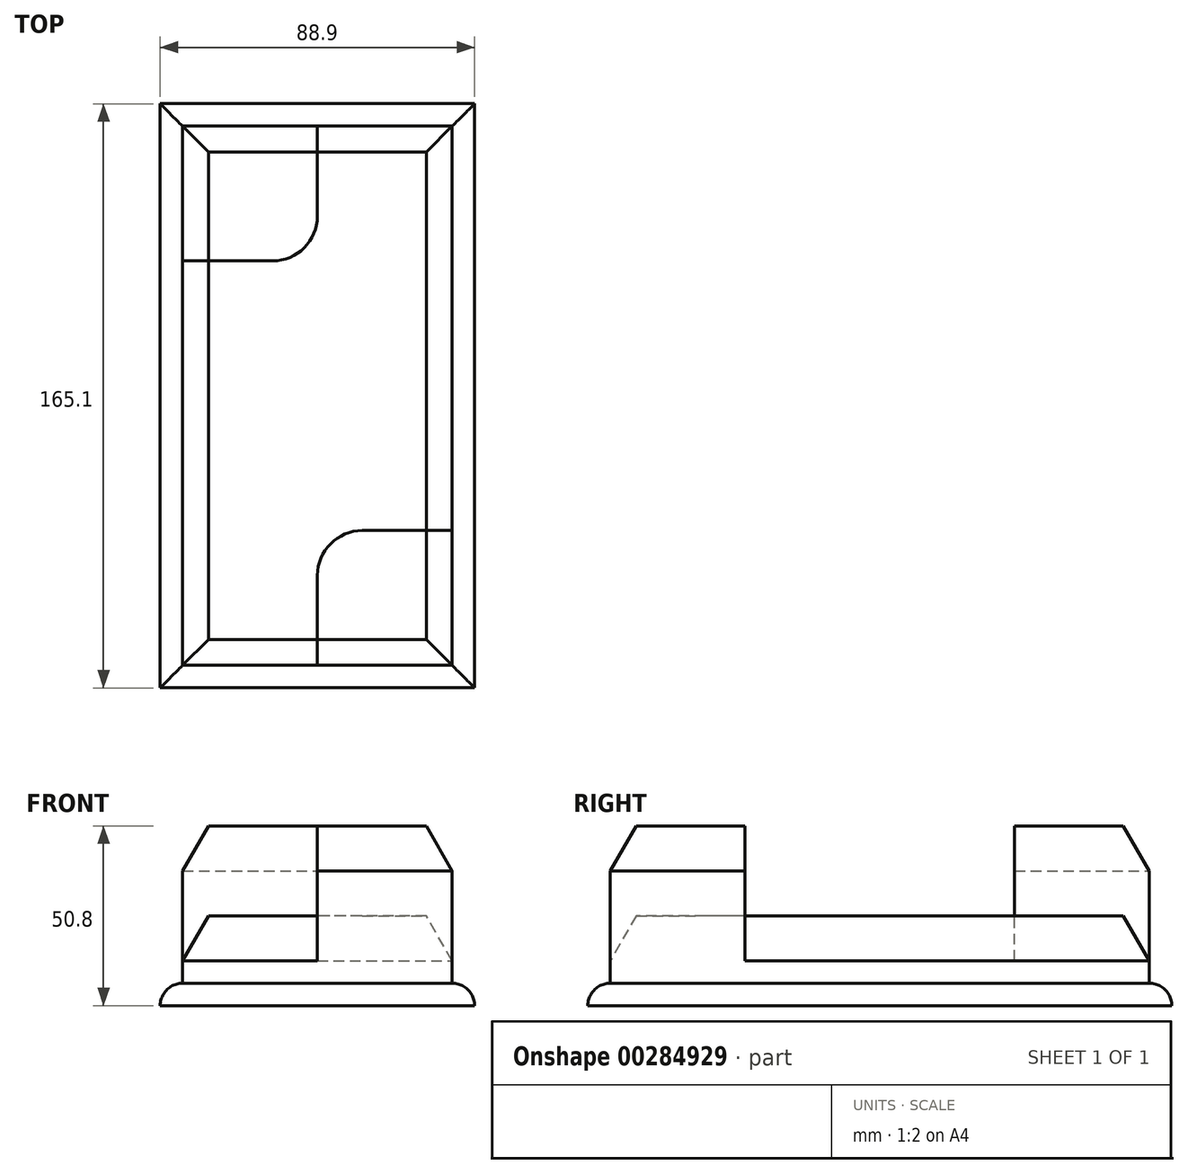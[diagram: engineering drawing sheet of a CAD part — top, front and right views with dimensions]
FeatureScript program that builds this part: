
annotation { "Feature Type Name" : "Feature", "Feature Type Description" : "" }
export const myFeature = defineFeature(function(context is Context, id is Id, definition is map)
    precondition{}
    {
        {
            var Q0;
            Q0=qCreatedBy(makeId("Top.planeOp"),FACE);
            var sketch = newSketch(context, id + "F0", { "sketchPlane" : qUnion([Q0])});
            skLineSegment(sketch, "E0", {"start": v(-43.8, 68.26) * mm, "end": v(-43.8, -84.14) * mm});
            skLineSegment(sketch, "E1", {"start": v(-43.8, -84.14) * mm, "end": v(32.4, -84.14) * mm});
            skLineSegment(sketch, "E2", {"start": v(32.4, -84.14) * mm, "end": v(32.4, 68.26) * mm});
            skLineSegment(sketch, "E3", {"start": v(32.4, 68.26) * mm, "end": v(-43.8, 68.26) * mm});
            skLineSegment(sketch, "E4", {"start": v(-5.7, 68.26) * mm, "end": v(-5.7, 42.86) * mm});
            skLineSegment(sketch, "E5", {"start": v(-18.4, 30.16) * mm, "end": v(-43.8, 30.16) * mm});
            skPoint(sketch, "E6.visualSharp", {"position": v(-5.7, 30.16) * mm});
            skArc(sketch, "E6.filletArc", {"start": v(-18.4, 30.16) * mm, "mid": v(-9.43, 33.88) * mm, "end": v(-5.7, 42.86) * mm});
            skLineSegment(sketch, "E7.0", {"start": v(38.74, 74.61) * mm, "end": v(-50.16, 74.61) * mm});
            skLineSegment(sketch, "E7.1", {"start": v(38.74, -90.49) * mm, "end": v(38.74, 74.61) * mm});
            skLineSegment(sketch, "E7.2", {"start": v(-50.16, -90.49) * mm, "end": v(38.74, -90.49) * mm});
            skLineSegment(sketch, "E7.3", {"start": v(-50.16, 74.61) * mm, "end": v(-50.16, -90.49) * mm});
            skLineSegment(sketch, "E8", {"start": v(-5.7, -84.14) * mm, "end": v(-5.7, -58.74) * mm});
            skLineSegment(sketch, "E9", {"start": v(7, -46.04) * mm, "end": v(32.4, -46.04) * mm});
            skPoint(sketch, "E10.visualSharp", {"position": v(-5.7, -46.04) * mm});
            skArc(sketch, "E10.filletArc", {"start": v(7, -46.04) * mm, "mid": v(-1.99, -49.76) * mm, "end": v(-5.7, -58.74) * mm});
            skSolve(sketch);
        }
        {
            var Q0;
            Q0 = qSketchRegion(id + "F0", true);
            extrude(context, id + "F1", {"entities" : qUnion([Q0]), "depth" : 6.35 * mm});
        }
        {
            var Q0;
            {var subQ8=sQuery(id+"F0.wireOp",EDGE,"E4");Q0=makeQuery(id+"F0.imprint","IMPRINT",FACE,{"disambiguationData":[TD([[makeQuery(id+"F0.imprint","IMPRINT",EDGE,{"derivedFrom":subQ8}),1.0]])]});}
            extrude(context, id + "F2", {"entities" : qUnion([Q0]), "operationType" : NewBodyOperationType.ADD, "depth" : 25.4 * mm});
        }
        {
            var Q0;
            {var subQ1=sQuery(id+"F0.wireOp",EDGE,"E4");Q0=makeQuery(id+"F0.imprint","IMPRINT",FACE,{"disambiguationData":[TD([[makeQuery(id+"F0.imprint","IMPRINT",EDGE,{"derivedFrom":subQ1}),-1.0]])]});}
            var Q1;
            {var subQ1=sQuery(id+"F0.wireOp",EDGE,"E8");Q1=makeQuery(id+"F0.imprint","IMPRINT",FACE,{"disambiguationData":[TD([[makeQuery(id+"F0.imprint","IMPRINT",EDGE,{"derivedFrom":subQ1}),-1.0]])]});}
            extrude(context, id + "F3", {"entities" : qUnion([Q0, Q1]), "operationType" : NewBodyOperationType.ADD, "depth" : 50.8 * mm});
        }
        {
            var Q0;
            Q0=makeQuery(id+"F3.opExtrude","CAP_EDGE",EDGE,{"disambiguationData":[OSD([sQuery(id+"F0.wireOp",EDGE,"E1")])],"isStart":false});
            var Q1;
            Q1=makeQuery(id+"F3.opExtrude","CAP_EDGE",EDGE,{"disambiguationData":[OSD([sQuery(id+"F0.wireOp",EDGE,"E3")])],"isStart":false});
            var Q2;
            Q2=makeQuery(id+"F3.opExtrude","CAP_EDGE",EDGE,{"disambiguationData":[OSD([sQuery(id+"F0.wireOp",EDGE,"E2")])],"isStart":false});
            var Q3;
            Q3=makeQuery(id+"F3.opExtrude","CAP_EDGE",EDGE,{"disambiguationData":[OSD([sQuery(id+"F0.wireOp",EDGE,"E0")])],"isStart":false});
            var Q4;
            Q4=makeQuery(id+"F2.opExtrude","CAP_EDGE",EDGE,{"disambiguationData":[OSD([sQuery(id+"F0.wireOp",EDGE,"E2")])],"isStart":false});
            var Q5;
            Q5=makeQuery(id+"F2.opExtrude","CAP_EDGE",EDGE,{"disambiguationData":[OSD([sQuery(id+"F0.wireOp",EDGE,"E0")])],"isStart":false});
            var Q6;
            Q6=makeQuery(id+"F2.opExtrude","CAP_EDGE",EDGE,{"disambiguationData":[OSD([sQuery(id+"F0.wireOp",EDGE,"E3")])],"isStart":false});
            var Q7;
            Q7=makeQuery(id+"F2.opExtrude","CAP_EDGE",EDGE,{"disambiguationData":[OSD([sQuery(id+"F0.wireOp",EDGE,"E1")])],"isStart":false});
            chamfer(context, id + "F4", {"entities" : qUnion([Q0, Q1, Q2, Q3, Q4, Q5, Q6, Q7]), "chamferType" : ChamferType.OFFSET_ANGLE, "width" : 12.7 * mm, "oppositeDirection" : true, "angle" : 30 * degree, "tangentPropagation" : true});
        }
        {
            var Q0;
            Q0=makeQuery(id+"F1.opExtrude","CAP_EDGE",EDGE,{"disambiguationData":[OSD([sQuery(id+"F0.wireOp",EDGE,"E7.1")])],"isStart":false});
            var Q1;
            Q1=makeQuery(id+"F1.opExtrude","CAP_EDGE",EDGE,{"disambiguationData":[OSD([sQuery(id+"F0.wireOp",EDGE,"E7.0")])],"isStart":false});
            var Q2;
            Q2=makeQuery(id+"F1.opExtrude","CAP_EDGE",EDGE,{"disambiguationData":[OSD([sQuery(id+"F0.wireOp",EDGE,"E7.3")])],"isStart":false});
            var Q3;
            Q3=makeQuery(id+"F1.opExtrude","CAP_EDGE",EDGE,{"disambiguationData":[OSD([sQuery(id+"F0.wireOp",EDGE,"E7.2")])],"isStart":false});
            fillet(context, id + "F5", {"entities" : qUnion([Q0, Q1, Q2, Q3]), "radius" : 6.35 * mm, "tangentPropagation" : true, "allowEdgeOverflow" : false});
        }
    });
